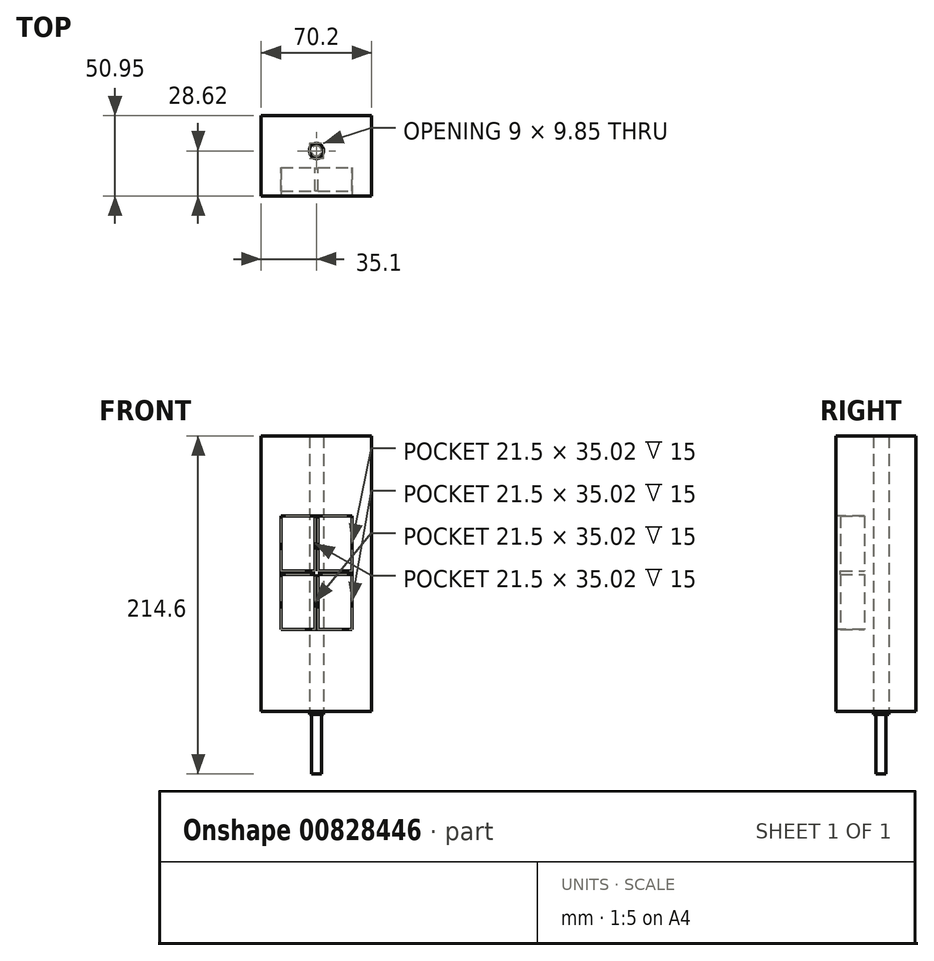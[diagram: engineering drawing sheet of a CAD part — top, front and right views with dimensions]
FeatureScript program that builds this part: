
annotation { "Feature Type Name" : "Feature", "Feature Type Description" : "" }
export const myFeature = defineFeature(function(context is Context, id is Id, definition is map)
    precondition{}
    {
        {
            var Q0;
            Q0=qCreatedBy(makeId("Top.planeOp"),FACE);
            var sketch = newSketch(context, id + "F0", { "sketchPlane" : qUnion([Q0])});
            skCircle(sketch, "E0", {"center": v(0, 0) * mm, "radius": 3.29 * mm});
            skSolve(sketch);
        }
        {
            var Q0;
            Q0 = qSketchRegion(id + "F0", true);
            extrude(context, id + "F1", {"entities" : qUnion([Q0]), "oppositeDirection" : true, "depth" : 39.6 * mm, "offsetDistance" : 25 * mm});
        }
        {
            var Q0;
            Q0=qCreatedBy(makeId("Top.planeOp"),FACE);
            var sketch = newSketch(context, id + "F2", { "sketchPlane" : qUnion([Q0])});
            skEllipse(sketch, "E1", {"center": v(0, 0) * mm, "majorRadius": 4.5 * mm, "minorRadius": 4.92 * mm, "majorAxis": v(1, 0)});
            skSolve(sketch);
        }
        {
            var Q0;
            Q0 = qSketchRegion(id + "F2", true);
            extrude(context, id + "F3", {"entities" : qUnion([Q0]), "operationType" : NewBodyOperationType.ADD, "oppositeDirection" : true, "depth" : 2 * mm, "offsetDistance" : 25 * mm});
        }
        {
            var Q0;
            Q0=makeQuery(id+"F3.boolean.opBoolean","MERGE",FACE,{"derivedFrom":[makeQuery(id+"F1.opExtrude","CAP_FACE",FACE,{"disambiguationData":[OSD([sQuery(id+"F0.wireOp",EDGE,"E0")])],"isStart":true}),makeQuery(id+"F3.opExtrude","CAP_FACE",FACE,{"disambiguationData":[OSD([sQuery(id+"F2.wireOp",EDGE,"E1")])],"isStart":true})]});
            var sketch = newSketch(context, id + "F4", { "sketchPlane" : qUnion([Q0])});
            skLineSegment(sketch, "E2", {"start": v(0, 4.92) * mm, "end": v(0, 22.32) * mm});
            skLineSegment(sketch, "E3", {"start": v(0, -4.92) * mm, "end": v(0, -28.62) * mm});
            skLineSegment(sketch, "E4", {"start": v(0, 0) * mm, "end": v(35.1, 0) * mm});
            skLineSegment(sketch, "E5", {"start": v(0, 0) * mm, "end": v(-35.1, 0) * mm});
            skLineSegment(sketch, "E6", {"start": v(0, 22.32) * mm, "end": v(-35.1, 22.32) * mm});
            skLineSegment(sketch, "E7", {"start": v(-35.1, 22.32) * mm, "end": v(-35.1, 0) * mm});
            skLineSegment(sketch, "E8", {"start": v(0, -28.62) * mm, "end": v(-35.1, -28.62) * mm});
            skLineSegment(sketch, "E9", {"start": v(-35.1, -28.62) * mm, "end": v(-35.1, 0) * mm});
            skLineSegment(sketch, "E10", {"start": v(0, -28.62) * mm, "end": v(35.1, -28.62) * mm});
            skLineSegment(sketch, "E11", {"start": v(0, 22.32) * mm, "end": v(35.1, 22.32) * mm});
            skLineSegment(sketch, "E12", {"start": v(35.1, 22.32) * mm, "end": v(35.1, -28.62) * mm});
            skSolve(sketch);
        }
        {
            var Q0;
            {var subQ4=sQuery(id+"F4.wireOp",EDGE,"E2");Q0=makeQuery(id+"F4.imprint","IMPRINT",FACE,{"disambiguationData":[TD([[makeQuery(id+"F4.imprint","IMPRINT",EDGE,{"derivedFrom":subQ4}),1.0]])]});}
            var Q1;
            {var subQ6=sQuery(id+"F4.wireOp",EDGE,"E3");Q1=makeQuery(id+"F4.imprint","IMPRINT",FACE,{"disambiguationData":[TD([[makeQuery(id+"F4.imprint","IMPRINT",EDGE,{"derivedFrom":subQ6}),1.0]])]});}
            var Q2;
            {var subQ4=sQuery(id+"F4.wireOp",EDGE,"E2");Q2=makeQuery(id+"F4.imprint","IMPRINT",FACE,{"disambiguationData":[TD([[makeQuery(id+"F4.imprint","IMPRINT",EDGE,{"derivedFrom":subQ4}),-1.0]])]});}
            var Q3;
            {var subQ4=sQuery(id+"F4.wireOp",EDGE,"E3");Q3=makeQuery(id+"F4.imprint","IMPRINT",FACE,{"disambiguationData":[TD([[makeQuery(id+"F4.imprint","IMPRINT",EDGE,{"derivedFrom":subQ4}),-1.0]])]});}
            extrude(context, id + "F5", {"entities" : qUnion([Q0, Q1, Q2, Q3]), "depth" : 175 * mm, "offsetDistance" : 25 * mm});
        }
        {
            var Q0;
            Q0=makeQuery(id+"F5.opExtrude","SWEPT_FACE",FACE,{"disambiguationData":[OSD([sQuery(id+"F4.wireOp",EDGE,"E8"),sQuery(id+"F4.wireOp",EDGE,"E10")])]});
            var sketch = newSketch(context, id + "F6", { "sketchPlane" : qUnion([Q0])});
            skLineSegment(sketch, "E13", {"start": v(0, 0) * mm, "end": v(0, 52.14) * mm});
            skLineSegment(sketch, "E14", {"start": v(0, 52.14) * mm, "end": v(-22.5, 52.14) * mm});
            skLineSegment(sketch, "E15.bottom", {"start": v(-22.5, 52.14) * mm, "end": v(22.5, 52.14) * mm});
            skLineSegment(sketch, "E15.top", {"start": v(-22.5, 124.18) * mm, "end": v(22.5, 124.18) * mm});
            skLineSegment(sketch, "E15.left", {"start": v(-22.5, 52.14) * mm, "end": v(-22.5, 124.18) * mm});
            skLineSegment(sketch, "E15.right", {"start": v(22.5, 52.14) * mm, "end": v(22.5, 124.18) * mm});
            skSolve(sketch);
        }
        {
            var Q0;
            Q0=makeQuery(id+"F6.imprint","IMPRINT",FACE,{"disambiguationData":[TD([[makeQuery(id+"F6.imprint","IMPRINT",EDGE,{"derivedFrom":sQuery(id+"F6.wireOp",EDGE,"E15.top")}),-1.0]])]});
            extrude(context, id + "F7", {"entities" : qUnion([Q0]), "operationType" : NewBodyOperationType.REMOVE, "oppositeDirection" : true, "depth" : 18 * mm, "offsetDistance" : 25 * mm});
        }
        {
            var Q0;
            Q0=makeQuery(id+"F7.boolean.opBoolean","COPY",FACE,{"derivedFrom":makeQuery(id+"F7.opExtrude","CAP_FACE",FACE,{"disambiguationData":[OSD([sQuery(id+"F6.wireOp",EDGE,"E15.bottom"),sQuery(id+"F6.wireOp",EDGE,"E15.top"),sQuery(id+"F6.wireOp",EDGE,"E15.left"),sQuery(id+"F6.wireOp",EDGE,"E15.right")])],"isStart":false})});
            var sketch = newSketch(context, id + "F8", { "sketchPlane" : qUnion([Q0])});
            skLineSegment(sketch, "E16", {"start": v(0, 52.14) * mm, "end": v(0, 124.18) * mm});
            skLineSegment(sketch, "E17", {"start": v(-22.5, 88.16) * mm, "end": v(22.5, 88.16) * mm});
            skLineSegment(sketch, "E18", {"start": v(0, 124.18) * mm, "end": v(-1, 124.18) * mm});
            skLineSegment(sketch, "E19", {"start": v(0, 124.18) * mm, "end": v(1, 124.18) * mm});
            skLineSegment(sketch, "E20", {"start": v(-22.5, 88.16) * mm, "end": v(-22.5, 89.16) * mm});
            skLineSegment(sketch, "E21", {"start": v(-22.5, 88.16) * mm, "end": v(-22.5, 87.16) * mm});
            skLineSegment(sketch, "E22", {"start": v(-22.5, 89.16) * mm, "end": v(22.5, 89.16) * mm});
            skLineSegment(sketch, "E23", {"start": v(-22.5, 87.16) * mm, "end": v(22.5, 87.16) * mm});
            skLineSegment(sketch, "E24", {"start": v(-1, 124.18) * mm, "end": v(-1, 52.14) * mm});
            skLineSegment(sketch, "E25", {"start": v(1, 124.18) * mm, "end": v(1, 52.14) * mm});
            skSolve(sketch);
        }
        {
            var Q0;
            {var subQ0=sQuery(id+"F8.wireOp",EDGE,"E18");Q0=makeQuery(id+"F8.imprint","IMPRINT",FACE,{"disambiguationData":[TD([[makeQuery(id+"F8.imprint","IMPRINT",EDGE,{"derivedFrom":subQ0}),-1.0]])]});}
            var Q1;
            {var subQ0=sQuery(id+"F8.wireOp",EDGE,"E19");Q1=makeQuery(id+"F8.imprint","IMPRINT",FACE,{"disambiguationData":[TD([[makeQuery(id+"F8.imprint","IMPRINT",EDGE,{"derivedFrom":subQ0}),-1.0]])]});}
            var Q2;
            {var subQ0=sQuery(id+"F8.wireOp",EDGE,"E17");var subQ1=sQuery(id+"F8.wireOp",EDGE,"E16");var subQ2=makeQuery(id+"F8.imprint","INTERSECT",VERTEX,{"derivedFrom":[subQ1,subQ0]});Q2=makeQuery(id+"F8.imprint","IMPRINT",FACE,{"disambiguationData":[TD([[makeQuery(id+"F8.imprint","IMPRINT",EDGE,{"disambiguationData":[TD([[subQ2,-1.0]])],"derivedFrom":subQ1}),1.0]])]});}
            var Q3;
            {var subQ0=sQuery(id+"F8.wireOp",EDGE,"E20");Q3=makeQuery(id+"F8.imprint","IMPRINT",FACE,{"disambiguationData":[TD([[makeQuery(id+"F8.imprint","IMPRINT",EDGE,{"derivedFrom":subQ0}),-1.0]])]});}
            var Q4;
            {var subQ0=sQuery(id+"F8.wireOp",EDGE,"E17");var subQ1=sQuery(id+"F8.wireOp",EDGE,"E16");var subQ2=makeQuery(id+"F8.imprint","INTERSECT",VERTEX,{"derivedFrom":[subQ1,subQ0]});Q4=makeQuery(id+"F8.imprint","IMPRINT",FACE,{"disambiguationData":[TD([[makeQuery(id+"F8.imprint","IMPRINT",EDGE,{"disambiguationData":[TD([[subQ2,-1.0]])],"derivedFrom":subQ1}),-1.0]])]});}
            var Q5;
            {var subQ0=sQuery(id+"F8.wireOp",EDGE,"E17");var subQ1=makeQuery(id+"F7.boolean.opBoolean","COPY",EDGE,{"derivedFrom":makeQuery(id+"F7.opExtrude","CAP_EDGE",EDGE,{"disambiguationData":[OSD([sQuery(id+"F6.wireOp",EDGE,"E15.right")])],"isStart":false})});var subQ2=makeQuery(id+"F8.imprint","INTERSECT",VERTEX,{"derivedFrom":[subQ1,subQ0]});Q5=makeQuery(id+"F8.imprint","IMPRINT",FACE,{"disambiguationData":[TD([[makeQuery(id+"F8.imprint","IMPRINT",EDGE,{"disambiguationData":[TD([[subQ2,1.0]])],"derivedFrom":subQ0}),1.0]])]});}
            var Q6;
            {var subQ0=sQuery(id+"F8.wireOp",EDGE,"E23");var subQ1=sQuery(id+"F8.wireOp",EDGE,"E16");var subQ2=makeQuery(id+"F8.imprint","INTERSECT",VERTEX,{"derivedFrom":[subQ1,subQ0]});Q6=makeQuery(id+"F8.imprint","IMPRINT",FACE,{"disambiguationData":[TD([[makeQuery(id+"F8.imprint","IMPRINT",EDGE,{"disambiguationData":[TD([[subQ2,-1.0]])],"derivedFrom":subQ1}),-1.0]])]});}
            var Q7;
            {var subQ0=sQuery(id+"F8.wireOp",EDGE,"E23");var subQ1=sQuery(id+"F8.wireOp",EDGE,"E16");var subQ2=makeQuery(id+"F8.imprint","INTERSECT",VERTEX,{"derivedFrom":[subQ1,subQ0]});Q7=makeQuery(id+"F8.imprint","IMPRINT",FACE,{"disambiguationData":[TD([[makeQuery(id+"F8.imprint","IMPRINT",EDGE,{"disambiguationData":[TD([[subQ2,-1.0]])],"derivedFrom":subQ1}),1.0]])]});}
            var Q8;
            {var subQ0=sQuery(id+"F8.wireOp",EDGE,"E21");Q8=makeQuery(id+"F8.imprint","IMPRINT",FACE,{"disambiguationData":[TD([[makeQuery(id+"F8.imprint","IMPRINT",EDGE,{"derivedFrom":subQ0}),-1.0]])]});}
            var Q9;
            {var subQ0=sQuery(id+"F8.wireOp",EDGE,"E17");var subQ1=makeQuery(id+"F7.boolean.opBoolean","COPY",EDGE,{"derivedFrom":makeQuery(id+"F7.opExtrude","CAP_EDGE",EDGE,{"disambiguationData":[OSD([sQuery(id+"F6.wireOp",EDGE,"E15.right")])],"isStart":false})});var subQ2=makeQuery(id+"F8.imprint","INTERSECT",VERTEX,{"derivedFrom":[subQ1,subQ0]});Q9=makeQuery(id+"F8.imprint","IMPRINT",FACE,{"disambiguationData":[TD([[makeQuery(id+"F8.imprint","IMPRINT",EDGE,{"disambiguationData":[TD([[subQ2,1.0]])],"derivedFrom":subQ0}),-1.0]])]});}
            var Q10;
            {var subQ0=sQuery(id+"F8.wireOp",EDGE,"E16");var subQ1=makeQuery(id+"F7.boolean.opBoolean","COPY",EDGE,{"derivedFrom":makeQuery(id+"F7.opExtrude","CAP_EDGE",EDGE,{"disambiguationData":[OSD([sQuery(id+"F6.wireOp",EDGE,"E15.bottom")])],"isStart":false})});var subQ2=makeQuery(id+"F8.imprint","INTERSECT",VERTEX,{"derivedFrom":[subQ1,subQ0]});Q10=makeQuery(id+"F8.imprint","IMPRINT",FACE,{"disambiguationData":[TD([[makeQuery(id+"F8.imprint","IMPRINT",EDGE,{"disambiguationData":[TD([[subQ2,-1.0]])],"derivedFrom":subQ0}),-1.0]])]});}
            var Q11;
            {var subQ0=sQuery(id+"F8.wireOp",EDGE,"E16");var subQ1=makeQuery(id+"F7.boolean.opBoolean","COPY",EDGE,{"derivedFrom":makeQuery(id+"F7.opExtrude","CAP_EDGE",EDGE,{"disambiguationData":[OSD([sQuery(id+"F6.wireOp",EDGE,"E15.bottom")])],"isStart":false})});var subQ2=makeQuery(id+"F8.imprint","INTERSECT",VERTEX,{"derivedFrom":[subQ1,subQ0]});Q11=makeQuery(id+"F8.imprint","IMPRINT",FACE,{"disambiguationData":[TD([[makeQuery(id+"F8.imprint","IMPRINT",EDGE,{"disambiguationData":[TD([[subQ2,-1.0]])],"derivedFrom":subQ0}),1.0]])]});}
            extrude(context, id + "F9", {"entities" : qUnion([Q0, Q1, Q2, Q3, Q4, Q5, Q6, Q7, Q8, Q9, Q10, Q11]), "operationType" : NewBodyOperationType.ADD, "depth" : 15 * mm, "offsetDistance" : 25 * mm});
        }
    });
